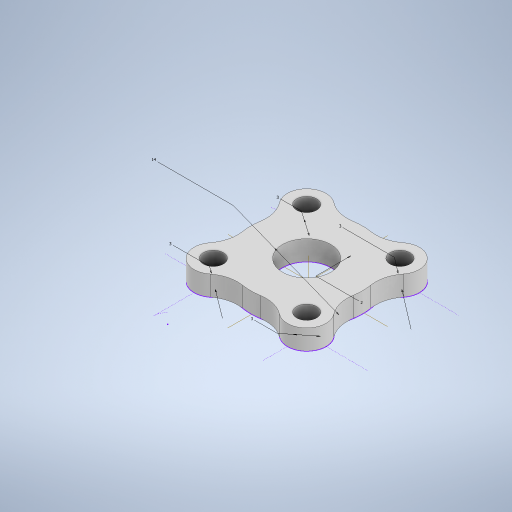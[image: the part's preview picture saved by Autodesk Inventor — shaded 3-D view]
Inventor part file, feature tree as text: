
AUTODESK INVENTOR PART (.ipt)
format: ipt  version: 2024.2 (Build 282272000, 272)  size: 309,760 bytes
history: native  units: mm
features: other x9, extrude x2, sketch x1
ambient origin geometry x8: Origin, YZ Plane, XZ Plane, XY Plane, X Axis, Y Axis, Z Axis, Center Point
bodies: Body1 (feature_tree)
feature tree (12):
  other  "Твердое тело1"
  sketch  "Эскиз1"
  extrude  "Выдавливание1"  Depth=3.0mm TaperAngle=0.0deg
  extrude  "Выдавливание3"  Depth=2.0mm
  other  "Сопряжение грани1"
  other  "Сопряжение грани2"
  other  "Сопряжение грани3"
  other  "Сопряжение грани4"
  other  "Сопряжение грани5"
  other  "Сопряжение грани6"
  other  "Сопряжение грани7"
  other  "Сопряжение грани8"
